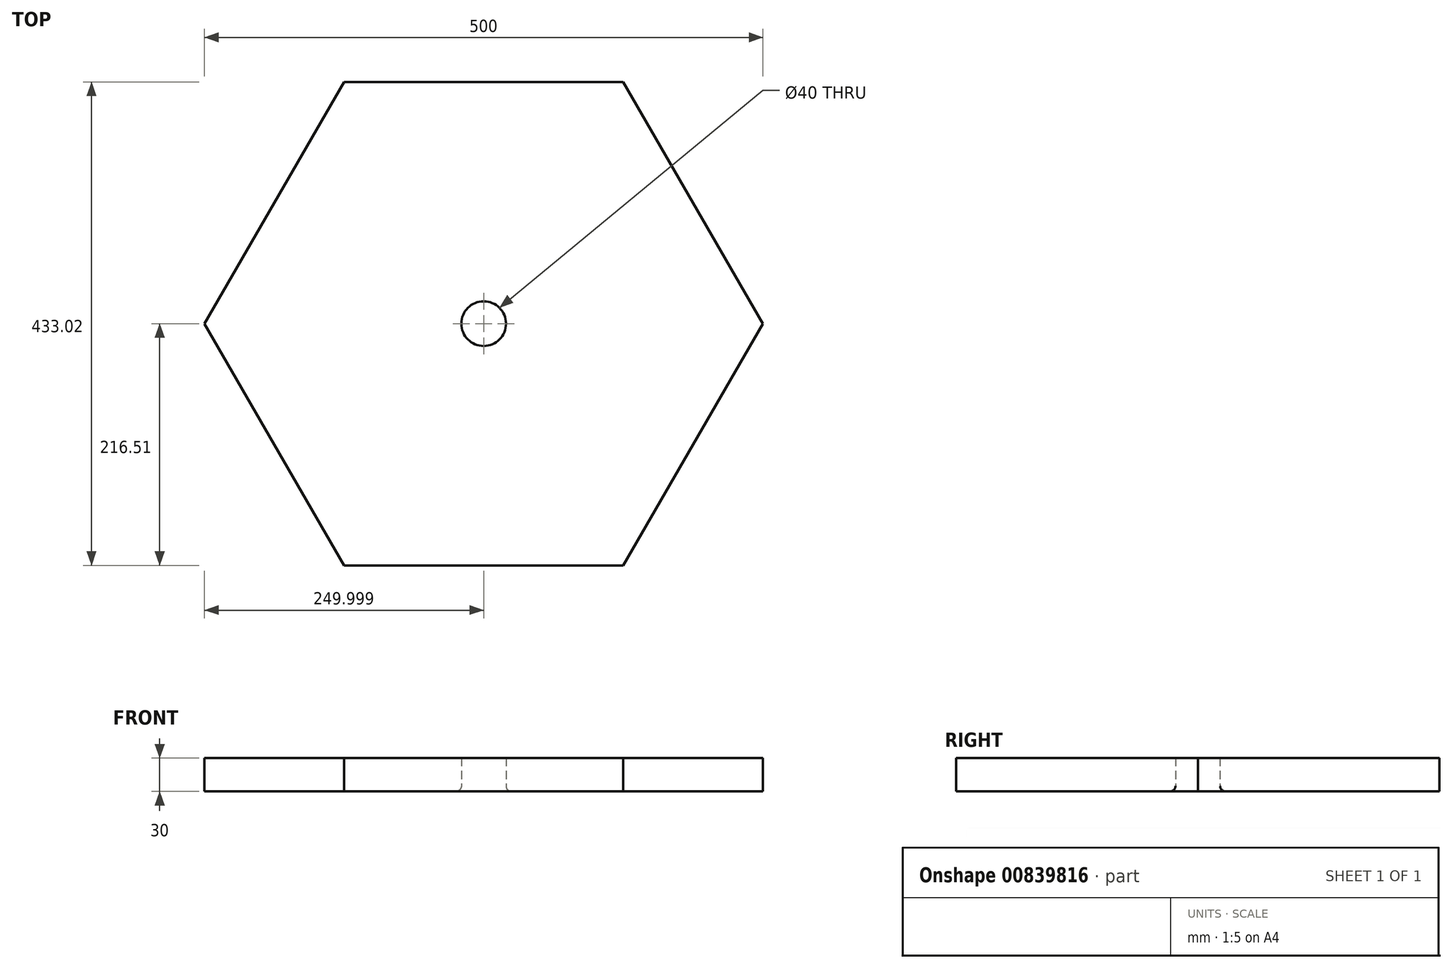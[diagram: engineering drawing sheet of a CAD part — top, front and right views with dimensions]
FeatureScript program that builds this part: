
annotation { "Feature Type Name" : "Feature", "Feature Type Description" : "" }
export const myFeature = defineFeature(function(context is Context, id is Id, definition is map)
    precondition{}
    {
        {
            var Q0;
            Q0=qCreatedBy(makeId("Top.planeOp"),FACE);
            var sketch = newSketch(context, id + "F0", { "sketchPlane" : qUnion([Q0])});
            skLineSegment(sketch, "E0", {"start": v(76.56, -635.43) * mm, "end": v(-48.44, -418.92) * mm});
            skLineSegment(sketch, "E1", {"start": v(-48.44, -418.92) * mm, "end": v(76.56, -202.41) * mm});
            skLineSegment(sketch, "E2", {"start": v(76.56, -202.41) * mm, "end": v(326.56, -202.41) * mm});
            skLineSegment(sketch, "E3", {"start": v(451.56, -418.92) * mm, "end": v(326.56, -202.41) * mm});
            skLineSegment(sketch, "E4", {"start": v(451.56, -418.92) * mm, "end": v(326.56, -635.43) * mm});
            skLineSegment(sketch, "E5", {"start": v(326.56, -635.43) * mm, "end": v(76.56, -635.43) * mm});
            skCircle(sketch, "E6", {"center": v(201.56, -418.92) * mm, "radius": 20 * mm});
            skSolve(sketch);
        }
        {
            var Q0;
            Q0=makeQuery(id+"F0.imprint","IMPRINT",FACE,{"disambiguationData":[TD([[makeQuery(id+"F0.imprint","IMPRINT",EDGE,{"derivedFrom":sQuery(id+"F0.wireOp",EDGE,"E0")}),-1.0]])]});
            extrude(context, id + "F1", {"entities" : qUnion([Q0]), "depth" : 30 * mm, "offsetDistance" : 25 * mm});
        }
        {
            var Q0;
            Q0=makeQuery(id+"F1.opExtrude","CAP_EDGE",EDGE,{"disambiguationData":[OSD([sQuery(id+"F0.wireOp",EDGE,"E6")])],"isStart":true});
            fillet(context, id + "F2", {"entities" : qUnion([Q0]), "radius" : 5 * mm, "tangentPropagation" : true, "allowEdgeOverflow" : false});
        }
    });
